# Revit family: PRD_AR_FlshCntrlDvcs_FlushPipeExtension_ACXF40031
name_source: partatom
category: Specialty Equipment
units: mm (PartAtom-declared; Revit-internal decimal feet)

## family parameters
Always vertical = Yes
Cut with Voids When Loaded = No
Enable Cutting in Views = No
Maintain Annotation Orientation = No
OmniClass Number = 23.45.05.14.99
OmniClass Title = Other Sanitary Washing Plumbing Fixtures
Part Type = Normal
Room Calculation Point = No
Round Connector Dimension = Use Diameter
Shared = No
Work Plane-Based = No

## types (1)
- ACXF4003
    AssetType = Fixed
    BIMObjectName = PRD_AR_FlushControlDevices_FlushPipeExtension_ACXF4003
    BodyMaterial = PRD_AR_PlasticMaterial
    Category = Pr_75_50_46_31, Flush control devices
    Default Elevation = 0 mm  [stored 0 ft]
    Description = Plastic flush pipe extension 28 x 1 x 400 mm.
    Export Type to IFC As = IfcPipeFittingType
    Features = Dimension  Ø 28x1 x 400  mm.
    FittingLossFactor = 0
    IfcExportAs = IfcPipeFittingType
    IfcExportType = USERDEFINED
    Manufacturer = KWC Group Management AG
    ManufacturerName = KWC Group Management AG
    ManufacturerURL = www.kwc-professional.com
    Material = Plastic
    Model = ACXF4003
    ModelNumber = 3600003801
    ModelReference = ACXF4003
    NBSDescription = Flush control devices
    NBSReference = 90-15-35/470
    Name = Flush pipe extension ACXF4003
    NominalDepth = 0 mm  [stored 0 ft]
    NominalHeight = 400 mm  [stored 1.31234 ft]
    NominalWidth = 0 mm  [stored 0 ft]
    PressureClass = 0.0 Pa
    PressureRange = 0.0 Pa
    Size = 30
    Status = New
    TemperatureRange = 0 °C
    Type IFC Predefined Type = USERDEFINED
    TypeOfFlushingPipe = Toilet flush pipe
    URL = www.kwc-professional.com
    Uniclass2015Code = Pr_75_50_46_31
    Uniclass2015Title = Flush control devices
    Uniclass2015Version = Products v1.36
    Version = 1
    WithOffset = No

note: [stored X ft] marks values corroborated as IEEE doubles in the binary element streams (Revit-internal decimal feet)

## geometry (parser evidence)
native form markers: Sweep x5
no freeform markers — native parametric forms only
